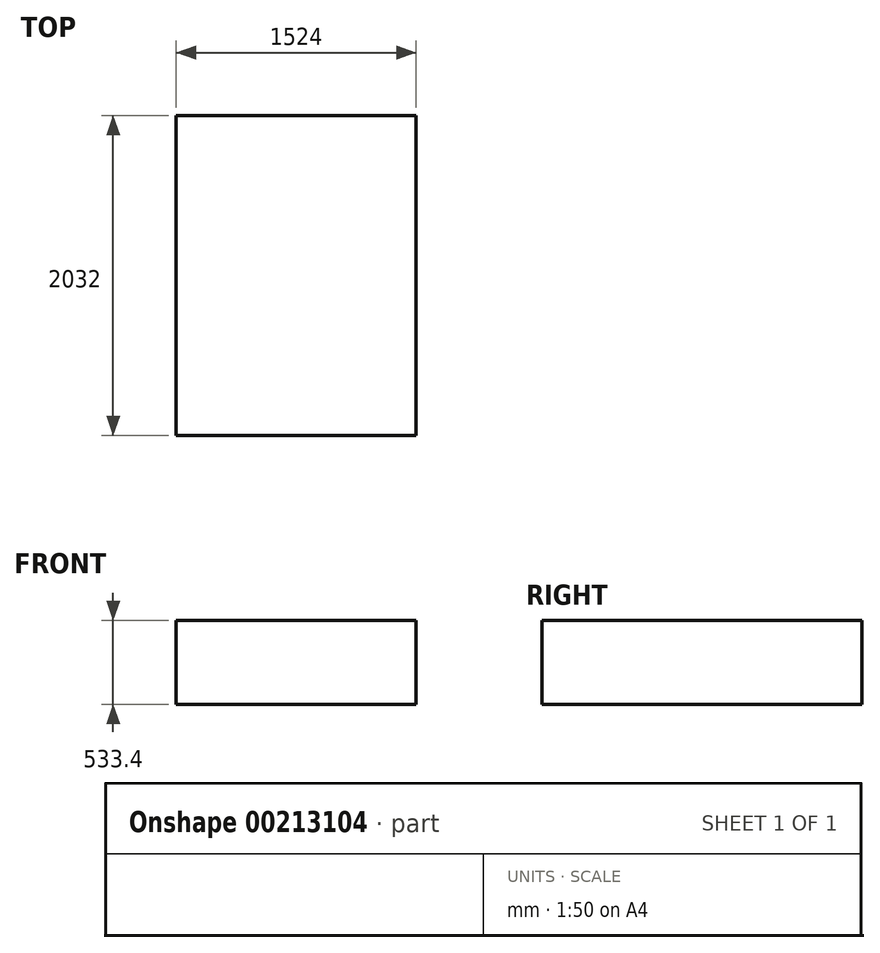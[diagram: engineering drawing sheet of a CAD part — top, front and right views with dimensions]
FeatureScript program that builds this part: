
annotation { "Feature Type Name" : "Feature", "Feature Type Description" : "" }
export const myFeature = defineFeature(function(context is Context, id is Id, definition is map)
    precondition{}
    {
        {
            var Q0;
            Q0=qCreatedBy(makeId("Front.planeOp"),FACE);
            var sketch = newSketch(context, id + "F0", { "sketchPlane" : qUnion([Q0])});
            skLineSegment(sketch, "E0.bottom", {"start": v(-33.05, 498.22) * mm, "end": v(1490.95, 498.22) * mm});
            skLineSegment(sketch, "E0.top", {"start": v(-33.05, -35.18) * mm, "end": v(1490.95, -35.18) * mm});
            skLineSegment(sketch, "E0.left", {"start": v(-33.05, 498.22) * mm, "end": v(-33.05, -35.18) * mm});
            skLineSegment(sketch, "E0.right", {"start": v(1490.95, 498.22) * mm, "end": v(1490.95, -35.18) * mm});
            skSolve(sketch);
        }
        {
            var Q0;
            Q0=makeQuery(id+"F0.imprint","IMPRINT",FACE,{"disambiguationData":[TD([[makeQuery(id+"F0.imprint","IMPRINT",EDGE,{"derivedFrom":sQuery(id+"F0.wireOp",EDGE,"E0.bottom")}),-1.0]])]});
            extrude(context, id + "F1", {"entities" : qUnion([Q0]), "depth" : 2032 * mm});
        }
    });
